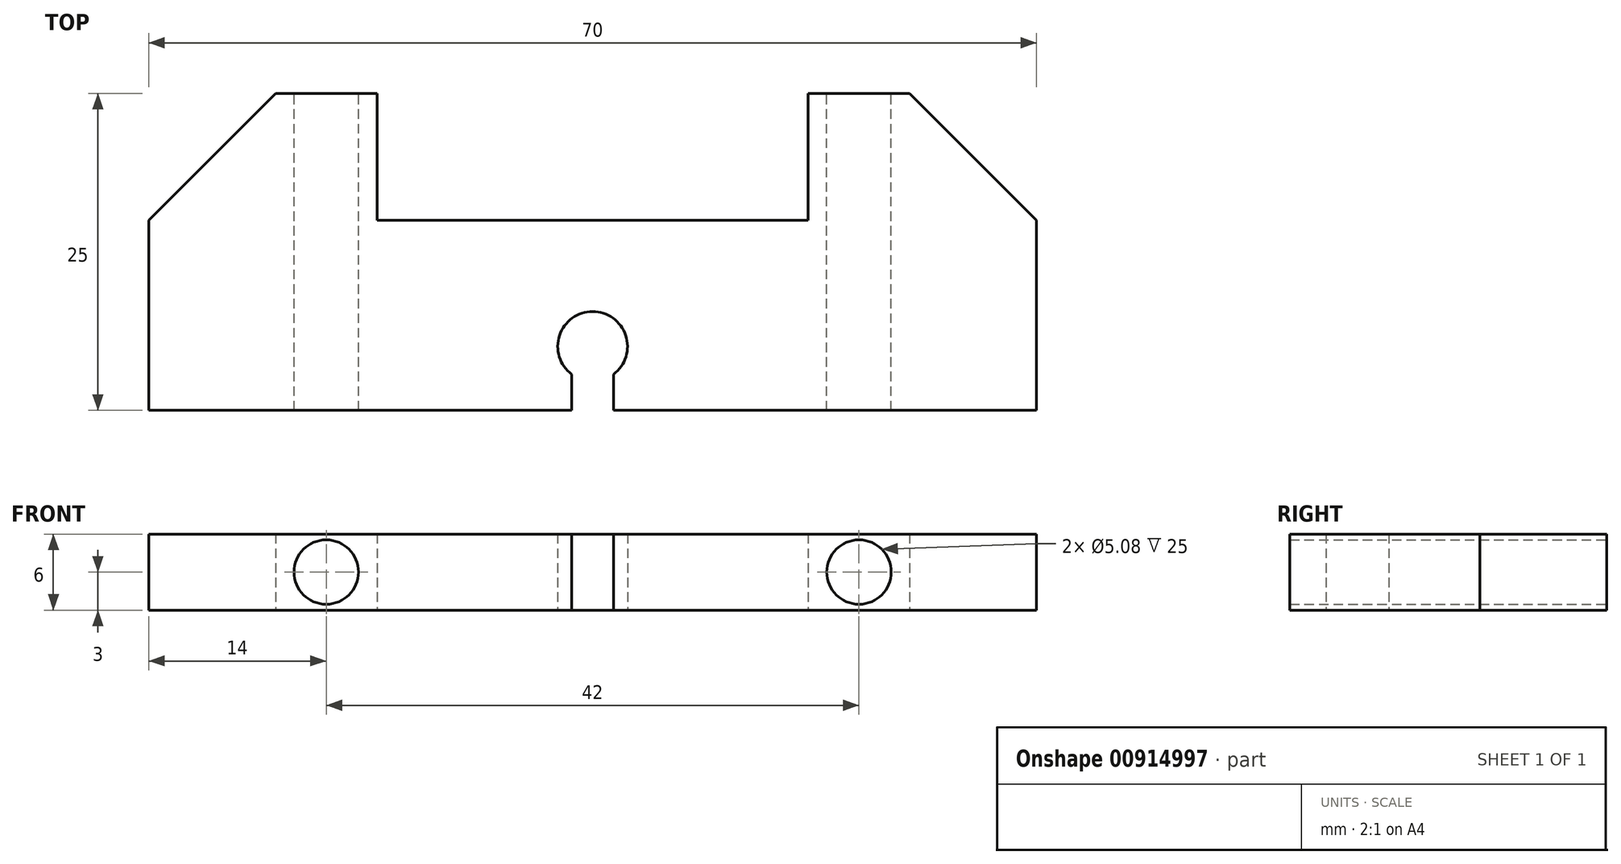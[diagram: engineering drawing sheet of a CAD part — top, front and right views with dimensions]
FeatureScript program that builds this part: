
annotation { "Feature Type Name" : "Feature", "Feature Type Description" : "" }
export const myFeature = defineFeature(function(context is Context, id is Id, definition is map)
    precondition{}
    {
        {
            var Q0;
            Q0=qCreatedBy(makeId("Top.planeOp"),FACE);
            var sketch = newSketch(context, id + "F0", { "sketchPlane" : qUnion([Q0])});
            skLineSegment(sketch, "E0", {"start": v(0, 0) * mm, "end": v(-35, 0) * mm});
            skLineSegment(sketch, "E1", {"start": v(0, 0) * mm, "end": v(35, 0) * mm});
            skLineSegment(sketch, "E2", {"start": v(-35, 0) * mm, "end": v(-35, 25) * mm});
            skLineSegment(sketch, "E3", {"start": v(-35, 25) * mm, "end": v(-17, 25) * mm});
            skLineSegment(sketch, "E4", {"start": v(-17, 25) * mm, "end": v(-17, 15) * mm});
            skLineSegment(sketch, "E5", {"start": v(-17, 15) * mm, "end": v(17, 15) * mm});
            skLineSegment(sketch, "E6", {"start": v(17, 15) * mm, "end": v(17, 25) * mm});
            skLineSegment(sketch, "E7", {"start": v(17, 25) * mm, "end": v(35, 25) * mm});
            skLineSegment(sketch, "E8", {"start": v(35, 25) * mm, "end": v(35, 0) * mm});
            skCircle(sketch, "E9", {"center": v(-21, 20) * mm, "radius": 2.5 * mm});
            skCircle(sketch, "E10", {"center": v(21, 20) * mm, "radius": 2.5 * mm});
            skPoint(sketch, "E10.centerSnap0", {"position": v(17, 20) * mm});
            skPoint(sketch, "E11", {"position": v(-17, 20) * mm});
            skPoint(sketch, "E12.endSnap0", {"position": v(35, 12.5) * mm});
            skPoint(sketch, "E13", {"position": v(-35, 15) * mm});
            skPoint(sketch, "E14", {"position": v(-35, 12.5) * mm});
            skLineSegment(sketch, "E15", {"start": v(-17, 15) * mm, "end": v(-35, 15) * mm, "construction": true});
            skLineSegment(sketch, "E16", {"start": v(17, 15) * mm, "end": v(35, 15) * mm, "construction": true});
            skPoint(sketch, "E17", {"position": v(35, 15) * mm});
            skLineSegment(sketch, "E18", {"start": v(-35, 15) * mm, "end": v(-25, 25) * mm});
            skLineSegment(sketch, "E19", {"start": v(35, 15) * mm, "end": v(25, 25) * mm});
            skCircle(sketch, "E20", {"center": v(0, 5.05) * mm, "radius": 2.75 * mm});
            skPoint(sketch, "E21", {"position": v(1.65, 2.85) * mm});
            skPoint(sketch, "E22", {"position": v(-1.65, 2.85) * mm});
            skLineSegment(sketch, "E23", {"start": v(1.65, 2.85) * mm, "end": v(1.65, 0) * mm});
            skLineSegment(sketch, "E24", {"start": v(-1.65, 2.85) * mm, "end": v(-1.65, 0) * mm});
            skPoint(sketch, "E25", {"position": v(0, 2.3) * mm});
            skLineSegment(sketch, "E26", {"start": v(0, 2.3) * mm, "end": v(0, 0) * mm, "construction": true});
            skLineSegment(sketch, "E27", {"start": v(25, 25) * mm, "end": v(25, 15) * mm, "construction": true});
            skLineSegment(sketch, "E28", {"start": v(-25, 25) * mm, "end": v(-25, 15) * mm, "construction": true});
            skLineSegment(sketch, "E29", {"start": v(21, 20) * mm, "end": v(17, 20) * mm, "construction": true});
            skLineSegment(sketch, "E30", {"start": v(21, 20) * mm, "end": v(25, 20) * mm, "construction": true});
            skPoint(sketch, "E31", {"position": v(21, 15) * mm});
            skLineSegment(sketch, "E32", {"start": v(21, 15) * mm, "end": v(21, 20) * mm, "construction": true});
            skLineSegment(sketch, "E33", {"start": v(-21, 20) * mm, "end": v(-17, 20) * mm, "construction": true});
            skLineSegment(sketch, "E34", {"start": v(-21, 20) * mm, "end": v(-21, 15) * mm, "construction": true});
            skLineSegment(sketch, "E35", {"start": v(-21, 20) * mm, "end": v(-25, 20) * mm, "construction": true});
            skSolve(sketch);
        }
        {
            var Q0;
            {var subQ3=sQuery(id+"F0.wireOp",EDGE,"E4");Q0=makeQuery(id+"F0.imprint","IMPRINT",FACE,{"disambiguationData":[TD([[makeQuery(id+"F0.imprint","IMPRINT",EDGE,{"derivedFrom":subQ3}),-1.0]])]});}
            var Q1;
            Q1=makeQuery(id+"F0.imprint","IMPRINT",FACE,{"disambiguationData":[TD([[makeQuery(id+"F0.imprint","IMPRINT",EDGE,{"derivedFrom":sQuery(id+"F0.wireOp",EDGE,"E10")}),1.0]])]});
            var Q2;
            Q2=makeQuery(id+"F0.imprint","IMPRINT",FACE,{"disambiguationData":[TD([[makeQuery(id+"F0.imprint","IMPRINT",EDGE,{"derivedFrom":sQuery(id+"F0.wireOp",EDGE,"E9")}),1.0]])]});
            extrude(context, id + "F1", {"entities" : qUnion([Q0, Q1, Q2]), "depth" : 6 * mm, "offsetDistance" : 25.4 * mm});
        }
        {
            var Q0;
            Q0=makeQuery(id+"F1.opExtrude","SWEPT_FACE",FACE,{"disambiguationData":[OSD([sQuery(id+"F0.wireOp",EDGE,"E7")])]});
            var sketch = newSketch(context, id + "F2", { "sketchPlane" : qUnion([Q0])});
            skCircle(sketch, "E36", {"center": v(21, 3) * mm, "radius": 2.5 * mm});
            skCircle(sketch, "E37", {"center": v(-21, 3) * mm, "radius": 2.5 * mm});
            skLineSegment(sketch, "E38", {"start": v(25, 6) * mm, "end": v(17, 6) * mm, "construction": true});
            skPoint(sketch, "E39", {"position": v(21, 6) * mm});
            skPoint(sketch, "E40", {"position": v(-21, 6) * mm});
            skLineSegment(sketch, "E41", {"start": v(-17, 6) * mm, "end": v(-25, 6) * mm, "construction": true});
            skLineSegment(sketch, "E42", {"start": v(-17, 6) * mm, "end": v(-17, 0) * mm, "construction": true});
            skPoint(sketch, "E43", {"position": v(-17, 3) * mm});
            skSolve(sketch);
        }
        {
            var Q0;
            Q0=sQuery(id+"F2.wireOp",VERTEX,"E36.center");
            var Q1;
            Q1=sQuery(id+"F2.wireOp",VERTEX,"E37.center");
            var Q2;
            Q2=makeQuery(id+"F1.opExtrude","SWEPT_BODY",BODY,{"disambiguationData":[OSD([sQuery(id+"F0.wireOp",EDGE,"E0"),sQuery(id+"F0.wireOp",EDGE,"E1"),sQuery(id+"F0.wireOp",EDGE,"E2"),sQuery(id+"F0.wireOp",EDGE,"E3"),sQuery(id+"F0.wireOp",EDGE,"E4"),sQuery(id+"F0.wireOp",EDGE,"E5"),sQuery(id+"F0.wireOp",EDGE,"E6"),sQuery(id+"F0.wireOp",EDGE,"E7"),sQuery(id+"F0.wireOp",EDGE,"E8"),sQuery(id+"F0.wireOp",EDGE,"E9"),sQuery(id+"F0.wireOp",EDGE,"E10"),sQuery(id+"F0.wireOp",EDGE,"E18"),sQuery(id+"F0.wireOp",EDGE,"E19"),sQuery(id+"F0.wireOp",EDGE,"E20"),sQuery(id+"F0.wireOp",EDGE,"E23"),sQuery(id+"F0.wireOp",EDGE,"E24")])]});
            hole(context, id + "F3", {"style" : HoleStyle.SIMPLE, "endStyle" : HoleEndStyle.THROUGH, "holeDiameter" : 5.08 * mm, "majorDiameter" : 6.35 * mm, "isTappedThrough" : true, "tappedDepth" : 12.7 * mm, "tapClearance" : 3, "locations" : qUnion([Q0, Q1]), "scope" : qUnion([Q2])});
        }
    });
